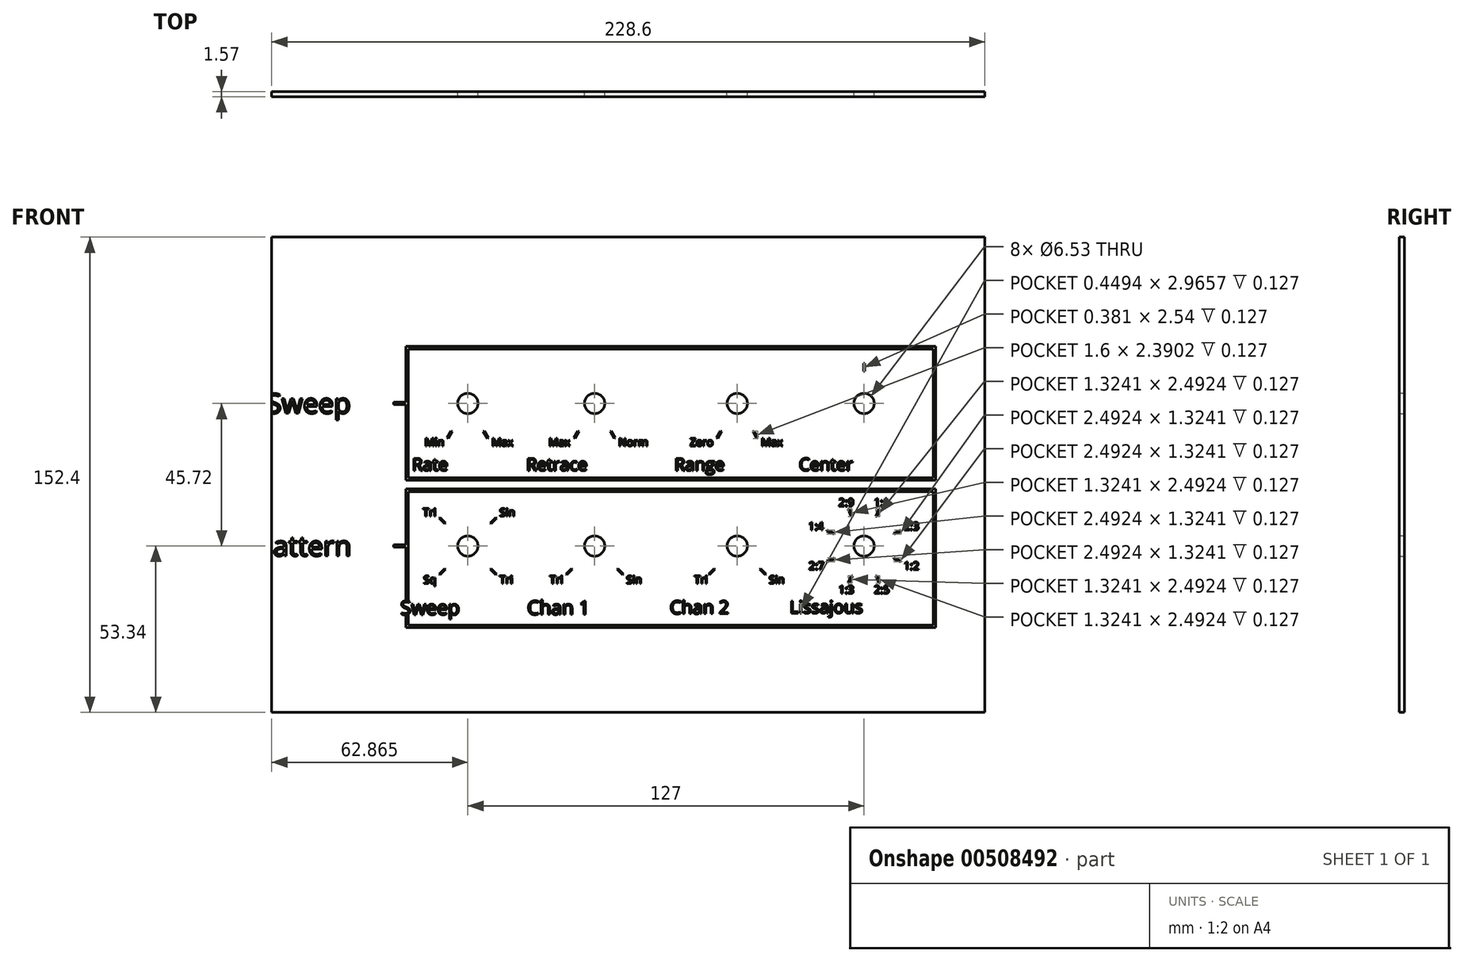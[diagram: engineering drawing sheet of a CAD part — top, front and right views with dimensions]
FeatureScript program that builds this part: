
annotation { "Feature Type Name" : "Feature", "Feature Type Description" : "" }
export const myFeature = defineFeature(function(context is Context, id is Id, definition is map)
    precondition{}
    {
        {
            var Q0;
            Q0=qCreatedBy(makeId("Front.planeOp"),FACE);
            var sketch = newSketch(context, id + "F0", { "sketchPlane" : qUnion([Q0])});
            skLineSegment(sketch, "E0.bottom", {"start": v(114.3, -76.2) * mm, "end": v(-114.3, -76.2) * mm});
            skLineSegment(sketch, "E0.top", {"start": v(114.3, 76.2) * mm, "end": v(-114.3, 76.2) * mm});
            skLineSegment(sketch, "E0.left", {"start": v(114.3, -76.2) * mm, "end": v(114.3, 76.2) * mm});
            skLineSegment(sketch, "E0.right", {"start": v(-114.3, -76.2) * mm, "end": v(-114.3, 76.2) * mm});
            skPoint(sketch, "E0.middle", {"position": v(0, 0) * mm});
            skSolve(sketch);
        }
        {
            var Q0;
            Q0 = qSketchRegion(id + "F0", true);
            extrude(context, id + "F1", {"entities" : qUnion([Q0]), "depth" : 1.57 * mm});
        }
        {
            var Q0;
            Q0=makeQuery(id+"F1.opExtrude","CAP_FACE",FACE,{"disambiguationData":[OSD([sQuery(id+"F0.wireOp",EDGE,"E0.bottom"),sQuery(id+"F0.wireOp",EDGE,"E0.top"),sQuery(id+"F0.wireOp",EDGE,"E0.left"),sQuery(id+"F0.wireOp",EDGE,"E0.right")])],"isStart":false});
            var sketch = newSketch(context, id + "F2", { "sketchPlane" : qUnion([Q0])});
            skLineSegment(sketch, "E1", {"start": v(0, 117.54) * mm, "end": v(0, -147.27) * mm, "construction": true});
            skPoint(sketch, "E1.startSnap0", {"position": v(0, 76.2) * mm});
            skLineSegment(sketch, "E2", {"start": v(-154.79, 0) * mm, "end": v(171.18, 0) * mm, "construction": true});
            skPoint(sketch, "E2.endSnap0", {"position": v(114.3, 0) * mm});
            skLineSegment(sketch, "E3", {"start": v(-51.44, 120.6) * mm, "end": v(-51.43, -147.27) * mm, "construction": true});
            skLineSegment(sketch, "E4", {"start": v(-10.8, 117.54) * mm, "end": v(-10.8, -147.27) * mm, "construction": true});
            skLineSegment(sketch, "E5", {"start": v(34.93, 117.54) * mm, "end": v(34.93, -147.27) * mm, "construction": true});
            skLineSegment(sketch, "E6", {"start": v(75.57, 117.54) * mm, "end": v(75.57, -147.27) * mm, "construction": true});
            skLineSegment(sketch, "E7", {"start": v(-154.79, 22.86) * mm, "end": v(171.18, 22.86) * mm, "construction": true});
            skLineSegment(sketch, "E8", {"start": v(-154.79, -22.86) * mm, "end": v(171.18, -22.86) * mm, "construction": true});
            skPoint(sketch, "E9", {"position": v(-51.44, 22.86) * mm});
            skPoint(sketch, "E10", {"position": v(-10.8, 22.86) * mm});
            skPoint(sketch, "E11", {"position": v(34.93, 22.86) * mm});
            skPoint(sketch, "E12", {"position": v(75.57, 22.86) * mm});
            skPoint(sketch, "E13", {"position": v(75.57, -22.86) * mm});
            skPoint(sketch, "E14", {"position": v(34.93, -22.86) * mm});
            skPoint(sketch, "E15", {"position": v(-10.8, -22.86) * mm});
            skPoint(sketch, "E16", {"position": v(-51.43, -22.86) * mm});
            skSolve(sketch);
        }
        {
            var Q0;
            Q0=sQuery(id+"F2.wireOp",VERTEX,"E9");
            var Q1;
            Q1=sQuery(id+"F2.wireOp",VERTEX,"E10");
            var Q2;
            Q2=sQuery(id+"F2.wireOp",VERTEX,"E11");
            var Q3;
            Q3=sQuery(id+"F2.wireOp",VERTEX,"E12");
            var Q4;
            Q4=sQuery(id+"F2.wireOp",VERTEX,"E13");
            var Q5;
            Q5=sQuery(id+"F2.wireOp",VERTEX,"E14");
            var Q6;
            Q6=sQuery(id+"F2.wireOp",VERTEX,"E15");
            var Q7;
            Q7=sQuery(id+"F2.wireOp",VERTEX,"E16");
            var Q8;
            Q8=makeQuery(id+"F1.opExtrude","SWEPT_BODY",BODY,{"disambiguationData":[OSD([sQuery(id+"F0.wireOp",EDGE,"E0.bottom"),sQuery(id+"F0.wireOp",EDGE,"E0.top"),sQuery(id+"F0.wireOp",EDGE,"E0.left"),sQuery(id+"F0.wireOp",EDGE,"E0.right")])]});
            hole(context, id + "F3", {"style" : HoleStyle.SIMPLE, "endStyle" : HoleEndStyle.THROUGH, "holeDiameter" : 6.53 * mm, "tappedDepth" : 19.05 * mm, "tapClearance" : 3, "locations" : qUnion([Q0, Q1, Q2, Q3, Q4, Q5, Q6, Q7]), "scope" : qUnion([Q8]), "startStyle" : HoleStartStyle.PART});
        }
        {
            var Q0;
            Q0=makeQuery(id+"F1.opExtrude","CAP_FACE",FACE,{"disambiguationData":[OSD([sQuery(id+"F0.wireOp",EDGE,"E0.bottom"),sQuery(id+"F0.wireOp",EDGE,"E0.top"),sQuery(id+"F0.wireOp",EDGE,"E0.left"),sQuery(id+"F0.wireOp",EDGE,"E0.right")])],"isStart":false});
            var sketch = newSketch(context, id + "F4", { "sketchPlane" : qUnion([Q0])});
            skText(sketch, "E17", { "text": "Sweep", "fontName": "OpenSans-Regular.ttf"});
            skText(sketch, "E18", { "text": "Chan 1", "fontName": "OpenSans-Regular.ttf"});
            skLineSegment(sketch, "E19", {"start": v(-51.44, 22.86) * mm, "end": v(-51.43, -69.4) * mm, "construction": true});
            skLineSegment(sketch, "E20", {"start": v(-10.8, 22.86) * mm, "end": v(-10.8, -69.78) * mm, "construction": true});
            skLineSegment(sketch, "E21", {"start": v(34.93, 22.86) * mm, "end": v(34.93, -69.78) * mm, "construction": true});
            skLineSegment(sketch, "E22", {"start": v(75.57, 22.86) * mm, "end": v(75.57, -65.32) * mm, "construction": true});
            skText(sketch, "E23", { "text": "Chan 2", "fontName": "OpenSans-Regular.ttf"});
            skText(sketch, "E24", { "text": "Lissajous", "fontName": "OpenSans-Regular.ttf"});
            skText(sketch, "E25", { "text": "Retrace", "fontName": "OpenSans-Regular.ttf"});
            skText(sketch, "E26", { "text": "Range", "fontName": "OpenSans-Regular.ttf"});
            skText(sketch, "E27", { "text": "Center", "fontName": "OpenSans-Regular.ttf"});
            skText(sketch, "E28", { "text": "Rate", "fontName": "OpenSans-Regular.ttf"});
            skLineSegment(sketch, "E29", {"start": v(-51.43, -22.86) * mm, "end": v(-101.2, -22.86) * mm, "construction": true});
            skLineSegment(sketch, "E30", {"start": v(-51.44, 22.86) * mm, "end": v(-100.19, 22.86) * mm, "construction": true});
            skText(sketch, "E31", { "text": "Sweep", "fontName": "OpenSans-Regular.ttf"});
            skText(sketch, "E32", { "text": "Pattern", "fontName": "OpenSans-Regular.ttf"});
            const initialGuessF4  = {"E17": [-0.07303, -0.04488, 1, 0, 0.00447], "E18": [-0.03238, -0.04485, 1, 0, 0.00444], "E23": [0.01334, -0.04462, 1, 0, 0.00421], "E24": [0.05173, -0.0444, 1, 0, 0.00399], "E25": [-0.03268, 0.00132, 1, 0, 0.00399], "E26": [0.0148, 0.00132, 1, 0, 0.00399], "E27": [0.0547, 0.00132, 1, 0, 0.00399], "E28": [-0.06932, 0.00132, 1, 0, 0.00399], "E31": [-0.11598, 0.01968, 1, 0, 0.00635], "E32": [-0.11916, -0.02604, 1, 0, 0.00635]};
            skSetInitialGuess(sketch, initialGuessF4);
            skSolve(sketch);
        }
        {
            var Q0;
            Q0 = qSketchRegion(id + "F4", true);
            extrude(context, id + "F5", {"entities" : qUnion([Q0]), "operationType" : NewBodyOperationType.REMOVE, "oppositeDirection" : true, "depth" : 0.13 * mm, "offsetDistance" : 25.4 * mm});
        }
        {
            var Q0;
            {var subQ0=sQuery(id+"F0.wireOp",EDGE,"E0.left");var subQ1=sQuery(id+"F0.wireOp",EDGE,"E0.top");var subQ2=sQuery(id+"F0.wireOp",EDGE,"E0.bottom");var subQ3=sQuery(id+"F0.wireOp",EDGE,"E0.right");Q0=makeQuery(id+"F5.boolean.opBoolean","SPLIT",FACE,{"disambiguationData":[TD([makeQuery(id+"F1.opExtrude","SWEPT_FACE",FACE,{"disambiguationData":[OSD([subQ2])]})])],"derivedFrom":makeQuery(id+"F1.opExtrude","CAP_FACE",FACE,{"disambiguationData":[OSD([subQ2,subQ1,subQ0,subQ3])],"isStart":false})});}
            var sketch = newSketch(context, id + "F6", { "sketchPlane" : qUnion([Q0])});
            skCircle(sketch, "E33", {"center": v(-51.43, -22.86) * mm, "radius": 10.32 * mm, "construction": true});
            skCircle(sketch, "E34", {"center": v(-51.43, -22.86) * mm, "radius": 12.7 * mm, "construction": true});
            skLineSegment(sketch, "E35", {"start": v(-51.43, -22.86) * mm, "end": v(-41.93, -13.35) * mm, "construction": true});
            skLineSegment(sketch, "E36", {"start": v(-51.43, -22.86) * mm, "end": v(-41.87, -32.42) * mm, "construction": true});
            skLineSegment(sketch, "E37", {"start": v(-51.43, -22.86) * mm, "end": v(-51.43, -8.06) * mm, "construction": true});
            skText(sketch, "E38", { "text": "Tri", "fontName": "OpenSans-Regular.ttf"});
            skLineSegment(sketch, "E39.bottom", {"start": v(-44, -30.02) * mm, "end": v(-42.2, -31.82) * mm});
            skLineSegment(sketch, "E39.top", {"start": v(-44.27, -30.29) * mm, "end": v(-42.48, -32.09) * mm});
            skLineSegment(sketch, "E39.left", {"start": v(-44, -30.02) * mm, "end": v(-44.27, -30.29) * mm});
            skLineSegment(sketch, "E39.right", {"start": v(-42.2, -31.82) * mm, "end": v(-42.48, -32.09) * mm});
            skLineSegment(sketch, "E40.bottom", {"start": v(-42.48, -13.63) * mm, "end": v(-44.27, -15.43) * mm});
            skLineSegment(sketch, "E40.top", {"start": v(-42.2, -13.9) * mm, "end": v(-44, -15.7) * mm});
            skLineSegment(sketch, "E40.left", {"start": v(-42.48, -13.63) * mm, "end": v(-42.2, -13.9) * mm});
            skLineSegment(sketch, "E40.right", {"start": v(-44.27, -15.43) * mm, "end": v(-44, -15.7) * mm});
            skCircle(sketch, "E41", {"center": v(75.57, -22.86) * mm, "radius": 10.32 * mm, "construction": true});
            skCircle(sketch, "E42", {"center": v(75.57, -22.86) * mm, "radius": 12.7 * mm, "construction": true});
            skLineSegment(sketch, "E43", {"start": v(75.57, -22.86) * mm, "end": v(75.57, 0) * mm, "construction": true});
            skLineSegment(sketch, "E44", {"start": v(75.57, -22.86) * mm, "end": v(84.9, -0.34) * mm, "construction": true});
            skLineSegment(sketch, "E45.1.0", {"start": v(75.57, -22.86) * mm, "end": v(66.24, -0.34) * mm, "construction": true});
            skLineSegment(sketch, "E45.2.0", {"start": v(75.57, -22.86) * mm, "end": v(53.05, -13.53) * mm, "construction": true});
            skLineSegment(sketch, "E45.3.0", {"start": v(75.57, -22.86) * mm, "end": v(53.05, -32.19) * mm, "construction": true});
            skLineSegment(sketch, "E45.4.0", {"start": v(75.57, -22.86) * mm, "end": v(66.24, -45.38) * mm, "construction": true});
            skLineSegment(sketch, "E45.5.0", {"start": v(75.57, -22.86) * mm, "end": v(84.9, -45.38) * mm, "construction": true});
            skLineSegment(sketch, "E45.6.0", {"start": v(75.57, -22.86) * mm, "end": v(98.08, -32.19) * mm, "construction": true});
            skLineSegment(sketch, "E45.7.0", {"start": v(75.57, -22.86) * mm, "end": v(98.08, -13.53) * mm, "construction": true});
            skLineSegment(sketch, "E46.bottom", {"start": v(79.34, -13.26) * mm, "end": v(80.3, -10.9) * mm});
            skLineSegment(sketch, "E46.top", {"start": v(79.69, -13.4) * mm, "end": v(80.66, -11.05) * mm});
            skLineSegment(sketch, "E46.left", {"start": v(79.34, -13.26) * mm, "end": v(79.69, -13.4) * mm});
            skLineSegment(sketch, "E46.right", {"start": v(80.3, -10.9) * mm, "end": v(80.66, -11.05) * mm});
            skLineSegment(sketch, "E47.1.0", {"start": v(85.17, -19.09) * mm, "end": v(87.52, -18.12) * mm});
            skLineSegment(sketch, "E47.1.1", {"start": v(85.02, -18.74) * mm, "end": v(87.37, -17.76) * mm});
            skLineSegment(sketch, "E47.1.2", {"start": v(87.37, -17.76) * mm, "end": v(87.52, -18.12) * mm});
            skLineSegment(sketch, "E47.1.3", {"start": v(85.02, -18.74) * mm, "end": v(85.17, -19.09) * mm});
            skLineSegment(sketch, "E47.2.0", {"start": v(85.02, -26.98) * mm, "end": v(87.37, -27.96) * mm});
            skLineSegment(sketch, "E47.2.1", {"start": v(85.17, -26.63) * mm, "end": v(87.52, -27.6) * mm});
            skLineSegment(sketch, "E47.2.2", {"start": v(87.52, -27.6) * mm, "end": v(87.37, -27.96) * mm});
            skLineSegment(sketch, "E47.2.3", {"start": v(85.17, -26.63) * mm, "end": v(85.02, -26.98) * mm});
            skLineSegment(sketch, "E47.3.0", {"start": v(79.34, -32.46) * mm, "end": v(80.3, -34.81) * mm});
            skLineSegment(sketch, "E47.3.1", {"start": v(79.69, -32.32) * mm, "end": v(80.66, -34.67) * mm});
            skLineSegment(sketch, "E47.3.2", {"start": v(80.66, -34.67) * mm, "end": v(80.3, -34.81) * mm});
            skLineSegment(sketch, "E47.3.3", {"start": v(79.69, -32.32) * mm, "end": v(79.34, -32.46) * mm});
            skLineSegment(sketch, "E47.4.0", {"start": v(71.44, -32.32) * mm, "end": v(70.47, -34.67) * mm});
            skLineSegment(sketch, "E47.4.1", {"start": v(71.8, -32.46) * mm, "end": v(70.82, -34.81) * mm});
            skLineSegment(sketch, "E47.4.2", {"start": v(70.82, -34.81) * mm, "end": v(70.47, -34.67) * mm});
            skLineSegment(sketch, "E47.4.3", {"start": v(71.8, -32.46) * mm, "end": v(71.44, -32.32) * mm});
            skLineSegment(sketch, "E47.5.0", {"start": v(65.96, -26.63) * mm, "end": v(63.61, -27.6) * mm});
            skLineSegment(sketch, "E47.5.1", {"start": v(66.1, -26.98) * mm, "end": v(63.76, -27.96) * mm});
            skLineSegment(sketch, "E47.5.2", {"start": v(63.76, -27.96) * mm, "end": v(63.61, -27.6) * mm});
            skLineSegment(sketch, "E47.5.3", {"start": v(66.1, -26.98) * mm, "end": v(65.96, -26.63) * mm});
            skLineSegment(sketch, "E47.6.0", {"start": v(66.1, -18.74) * mm, "end": v(63.76, -17.76) * mm});
            skLineSegment(sketch, "E47.6.1", {"start": v(65.96, -19.09) * mm, "end": v(63.61, -18.12) * mm});
            skLineSegment(sketch, "E47.6.2", {"start": v(63.61, -18.12) * mm, "end": v(63.76, -17.76) * mm});
            skLineSegment(sketch, "E47.6.3", {"start": v(65.96, -19.09) * mm, "end": v(66.1, -18.74) * mm});
            skLineSegment(sketch, "E47.7.0", {"start": v(71.8, -13.26) * mm, "end": v(70.82, -10.9) * mm});
            skLineSegment(sketch, "E47.7.1", {"start": v(71.44, -13.4) * mm, "end": v(70.47, -11.05) * mm});
            skLineSegment(sketch, "E47.7.2", {"start": v(70.47, -11.05) * mm, "end": v(70.82, -10.9) * mm});
            skLineSegment(sketch, "E47.7.3", {"start": v(71.44, -13.4) * mm, "end": v(71.8, -13.26) * mm});
            skLineSegment(sketch, "E47.anchor1", {"start": v(75.57, -22.86) * mm, "end": v(79.69, -13.4) * mm, "construction": true});
            skLineSegment(sketch, "E47.anchor2", {"start": v(75.57, -22.86) * mm, "end": v(71.8, -13.26) * mm, "construction": true});
            skText(sketch, "E48", { "text": "2:5", "fontName": "OpenSans-Regular.ttf"});
            skText(sketch, "E49", { "text": "1:3", "fontName": "OpenSans-Regular.ttf"});
            skText(sketch, "E50", { "text": "2:7", "fontName": "OpenSans-Regular.ttf"});
            skText(sketch, "E51", { "text": "1:4", "fontName": "OpenSans-Regular.ttf"});
            skText(sketch, "E52", { "text": "2:9", "fontName": "OpenSans-Regular.ttf"});
            skText(sketch, "E53", { "text": "1:1", "fontName": "OpenSans-Regular.ttf"});
            skText(sketch, "E54", { "text": "2:3", "fontName": "OpenSans-Regular.ttf"});
            skText(sketch, "E55", { "text": "1:2", "fontName": "OpenSans-Regular.ttf"});
            skLineSegment(sketch, "E56", {"start": v(-10.8, -22.86) * mm, "end": v(-10.8, -39.67) * mm, "construction": true});
            skLineSegment(sketch, "E57", {"start": v(34.93, -22.86) * mm, "end": v(34.93, -39.28) * mm, "construction": true});
            skCircle(sketch, "E58", {"center": v(-10.8, -22.86) * mm, "radius": 10.32 * mm, "construction": true});
            skCircle(sketch, "E59", {"center": v(-10.8, -22.86) * mm, "radius": 12.7 * mm, "construction": true});
            skCircle(sketch, "E60", {"center": v(34.93, -22.86) * mm, "radius": 10.32 * mm, "construction": true});
            skCircle(sketch, "E61", {"center": v(34.93, -22.86) * mm, "radius": 12.7 * mm, "construction": true});
            skLineSegment(sketch, "E62", {"start": v(-51.43, -22.86) * mm, "end": v(-65.5, -36.92) * mm, "construction": true});
            skLineSegment(sketch, "E63", {"start": v(-10.8, -22.86) * mm, "end": v(-24.75, -36.82) * mm, "construction": true});
            skLineSegment(sketch, "E64", {"start": v(-10.8, -22.86) * mm, "end": v(3.44, -37.1) * mm, "construction": true});
            skLineSegment(sketch, "E65", {"start": v(34.93, -22.86) * mm, "end": v(21.23, -36.55) * mm, "construction": true});
            skLineSegment(sketch, "E66", {"start": v(34.93, -22.86) * mm, "end": v(49.67, -37.6) * mm, "construction": true});
            skLineSegment(sketch, "E67.bottom", {"start": v(25.7, -31.82) * mm, "end": v(27.5, -30.02) * mm});
            skLineSegment(sketch, "E67.top", {"start": v(25.97, -32.09) * mm, "end": v(27.76, -30.29) * mm});
            skLineSegment(sketch, "E67.left", {"start": v(25.7, -31.82) * mm, "end": v(25.97, -32.09) * mm});
            skLineSegment(sketch, "E67.right", {"start": v(27.5, -30.02) * mm, "end": v(27.76, -30.29) * mm});
            skLineSegment(sketch, "E68.bottom", {"start": v(42.35, -30.02) * mm, "end": v(44.15, -31.82) * mm});
            skLineSegment(sketch, "E68.top", {"start": v(42.09, -30.29) * mm, "end": v(43.88, -32.09) * mm});
            skLineSegment(sketch, "E68.left", {"start": v(42.35, -30.02) * mm, "end": v(42.09, -30.29) * mm});
            skLineSegment(sketch, "E68.right", {"start": v(44.15, -31.82) * mm, "end": v(43.88, -32.09) * mm});
            skLineSegment(sketch, "E69.bottom", {"start": v(-20.02, -31.82) * mm, "end": v(-18.22, -30.02) * mm});
            skLineSegment(sketch, "E69.top", {"start": v(-19.75, -32.09) * mm, "end": v(-17.96, -30.29) * mm});
            skLineSegment(sketch, "E69.left", {"start": v(-20.02, -31.82) * mm, "end": v(-19.75, -32.09) * mm});
            skLineSegment(sketch, "E69.right", {"start": v(-18.22, -30.02) * mm, "end": v(-17.96, -30.29) * mm});
            skLineSegment(sketch, "E70.bottom", {"start": v(-3.37, -30.02) * mm, "end": v(-1.57, -31.82) * mm});
            skLineSegment(sketch, "E70.top", {"start": v(-3.63, -30.29) * mm, "end": v(-1.84, -32.09) * mm});
            skLineSegment(sketch, "E70.left", {"start": v(-3.37, -30.02) * mm, "end": v(-3.63, -30.29) * mm});
            skLineSegment(sketch, "E70.right", {"start": v(-1.57, -31.82) * mm, "end": v(-1.84, -32.09) * mm});
            skLineSegment(sketch, "E71.bottom", {"start": v(-60.66, -31.82) * mm, "end": v(-58.86, -30.02) * mm});
            skLineSegment(sketch, "E71.top", {"start": v(-60.4, -32.09) * mm, "end": v(-58.6, -30.29) * mm});
            skLineSegment(sketch, "E71.left", {"start": v(-60.66, -31.82) * mm, "end": v(-60.4, -32.09) * mm});
            skLineSegment(sketch, "E71.right", {"start": v(-58.86, -30.02) * mm, "end": v(-58.6, -30.29) * mm});
            skText(sketch, "E72", { "text": "Sin", "fontName": "OpenSans-Regular.ttf"});
            skText(sketch, "E73", { "text": "Sq", "fontName": "OpenSans-Regular.ttf"});
            skText(sketch, "E74", { "text": "Tri", "fontName": "OpenSans-Regular.ttf"});
            skText(sketch, "E75", { "text": "Sin", "fontName": "OpenSans-Regular.ttf"});
            skText(sketch, "E76", { "text": "Sin", "fontName": "OpenSans-Regular.ttf"});
            skText(sketch, "E77", { "text": "Tri", "fontName": "OpenSans-Regular.ttf"});
            skCircle(sketch, "E78", {"center": v(-51.44, 22.86) * mm, "radius": 10.32 * mm, "construction": true});
            skCircle(sketch, "E79", {"center": v(-51.44, 22.86) * mm, "radius": 12.7 * mm, "construction": true});
            skCircle(sketch, "E80", {"center": v(-10.8, 22.86) * mm, "radius": 10.32 * mm, "construction": true});
            skCircle(sketch, "E81", {"center": v(34.93, 22.86) * mm, "radius": 10.32 * mm, "construction": true});
            skCircle(sketch, "E82", {"center": v(75.57, 22.86) * mm, "radius": 10.32 * mm, "construction": true});
            skCircle(sketch, "E83", {"center": v(-10.8, 22.86) * mm, "radius": 12.7 * mm, "construction": true});
            skCircle(sketch, "E84", {"center": v(34.93, 22.86) * mm, "radius": 12.7 * mm, "construction": true});
            skCircle(sketch, "E85", {"center": v(75.57, 22.86) * mm, "radius": 12.7 * mm, "construction": true});
            skLineSegment(sketch, "E86", {"start": v(-10.8, 22.86) * mm, "end": v(-10.8, 0) * mm, "construction": true});
            skLineSegment(sketch, "E87", {"start": v(-10.8, 22.86) * mm, "end": v(-23.44, 0.97) * mm, "construction": true});
            skLineSegment(sketch, "E88", {"start": v(-10.8, 22.86) * mm, "end": v(2.14, 0.45) * mm, "construction": true});
            skLineSegment(sketch, "E89.bottom", {"start": v(-17.39, 11.82) * mm, "end": v(-16.12, 14.02) * mm});
            skLineSegment(sketch, "E89.top", {"start": v(-17.06, 11.63) * mm, "end": v(-15.79, 13.83) * mm});
            skLineSegment(sketch, "E89.left", {"start": v(-17.39, 11.82) * mm, "end": v(-17.06, 11.63) * mm});
            skLineSegment(sketch, "E89.right", {"start": v(-16.12, 14.02) * mm, "end": v(-15.79, 13.83) * mm});
            skLineSegment(sketch, "E90.bottom", {"start": v(-5.47, 14.02) * mm, "end": v(-4.2, 11.82) * mm});
            skLineSegment(sketch, "E90.top", {"start": v(-5.8, 13.83) * mm, "end": v(-4.53, 11.63) * mm});
            skLineSegment(sketch, "E90.left", {"start": v(-5.47, 14.02) * mm, "end": v(-5.8, 13.83) * mm});
            skLineSegment(sketch, "E90.right", {"start": v(-4.2, 11.82) * mm, "end": v(-4.53, 11.63) * mm});
            skText(sketch, "E91", { "text": "Norm", "fontName": "OpenSans-Regular.ttf"});
            skText(sketch, "E92", { "text": "Max", "fontName": "OpenSans-Regular.ttf"});
            skLineSegment(sketch, "E93", {"start": v(-51.43, 22.86) * mm, "end": v(-51.43, 6.58) * mm, "construction": true});
            skLineSegment(sketch, "E94", {"start": v(-51.44, 22.86) * mm, "end": v(-60.83, 6.58) * mm, "construction": true});
            skLineSegment(sketch, "E95", {"start": v(-51.44, 22.86) * mm, "end": v(-42.04, 6.58) * mm, "construction": true});
            skLineSegment(sketch, "E96.bottom", {"start": v(-58.03, 11.82) * mm, "end": v(-56.76, 14.02) * mm});
            skLineSegment(sketch, "E96.top", {"start": v(-57.7, 11.63) * mm, "end": v(-56.43, 13.83) * mm});
            skLineSegment(sketch, "E96.left", {"start": v(-58.03, 11.82) * mm, "end": v(-57.7, 11.63) * mm});
            skLineSegment(sketch, "E96.right", {"start": v(-56.76, 14.02) * mm, "end": v(-56.43, 13.83) * mm});
            skLineSegment(sketch, "E97.bottom", {"start": v(-46.11, 14.02) * mm, "end": v(-44.84, 11.82) * mm});
            skLineSegment(sketch, "E97.top", {"start": v(-46.44, 13.83) * mm, "end": v(-45.17, 11.63) * mm});
            skLineSegment(sketch, "E97.left", {"start": v(-46.11, 14.02) * mm, "end": v(-46.44, 13.83) * mm});
            skLineSegment(sketch, "E97.right", {"start": v(-44.84, 11.82) * mm, "end": v(-45.17, 11.63) * mm});
            skText(sketch, "E98", { "text": "Min", "fontName": "OpenSans-Regular.ttf"});
            skText(sketch, "E99", { "text": "Max", "fontName": "OpenSans-Regular.ttf"});
            skLineSegment(sketch, "E100", {"start": v(75.57, 22.86) * mm, "end": v(75.57, 41.9) * mm, "construction": true});
            skLineSegment(sketch, "E101.bottom", {"start": v(75.37, 35.72) * mm, "end": v(75.76, 35.72) * mm});
            skLineSegment(sketch, "E101.top", {"start": v(75.37, 33.18) * mm, "end": v(75.76, 33.18) * mm});
            skLineSegment(sketch, "E101.left", {"start": v(75.37, 35.72) * mm, "end": v(75.37, 33.18) * mm});
            skLineSegment(sketch, "E101.right", {"start": v(75.76, 35.72) * mm, "end": v(75.76, 33.18) * mm});
            skLineSegment(sketch, "E102", {"start": v(34.93, 22.86) * mm, "end": v(34.93, 3.94) * mm, "construction": true});
            skLineSegment(sketch, "E103", {"start": v(34.92, 22.86) * mm, "end": v(24, 3.94) * mm, "construction": true});
            skLineSegment(sketch, "E104", {"start": v(34.93, 22.86) * mm, "end": v(45.85, 3.94) * mm});
            skLineSegment(sketch, "E105.bottom", {"start": v(28.33, 11.82) * mm, "end": v(29.6, 14.02) * mm});
            skLineSegment(sketch, "E105.top", {"start": v(28.66, 11.63) * mm, "end": v(29.93, 13.83) * mm});
            skLineSegment(sketch, "E105.left", {"start": v(28.33, 11.82) * mm, "end": v(28.66, 11.63) * mm});
            skLineSegment(sketch, "E105.right", {"start": v(29.6, 14.02) * mm, "end": v(29.93, 13.83) * mm});
            skLineSegment(sketch, "E106.bottom", {"start": v(40.25, 14.02) * mm, "end": v(41.52, 11.82) * mm});
            skLineSegment(sketch, "E106.top", {"start": v(39.92, 13.83) * mm, "end": v(41.19, 11.63) * mm});
            skLineSegment(sketch, "E106.left", {"start": v(40.25, 14.02) * mm, "end": v(39.92, 13.83) * mm});
            skLineSegment(sketch, "E106.right", {"start": v(41.52, 11.82) * mm, "end": v(41.19, 11.63) * mm});
            skText(sketch, "E107", { "text": "Max", "fontName": "OpenSans-Regular.ttf"});
            skText(sketch, "E108", { "text": "Zero", "fontName": "OpenSans-Regular.ttf"});
            skLineSegment(sketch, "E109", {"start": v(-51.43, -22.86) * mm, "end": v(-63.42, -10.87) * mm, "construction": true});
            skLineSegment(sketch, "E110.bottom", {"start": v(-60.4, -13.63) * mm, "end": v(-58.6, -15.43) * mm});
            skLineSegment(sketch, "E110.top", {"start": v(-60.66, -13.9) * mm, "end": v(-58.86, -15.7) * mm});
            skLineSegment(sketch, "E110.left", {"start": v(-60.4, -13.63) * mm, "end": v(-60.66, -13.9) * mm});
            skLineSegment(sketch, "E110.right", {"start": v(-58.6, -15.43) * mm, "end": v(-58.86, -15.7) * mm});
            skText(sketch, "E111", { "text": "Tri", "fontName": "OpenSans-Regular.ttf"});
            const initialGuessF6  = {"E38": [-0.04127, -0.03493, 1, 0, 0.00254], "E48": [0.07874, -0.0381, 1, 0, 0.00254], "E49": [0.0674, -0.0381, 1, 0, 0.00254], "E50": [0.05784, -0.03048, 1, 0, 0.00254], "E51": [0.05773, -0.01778, 1, 0, 0.00254], "E52": [0.06738, -0.01016, 1, 0, 0.00254], "E53": [0.07874, -0.01016, 1, 0, 0.00254], "E54": [0.08827, -0.01778, 1, 0, 0.00254], "E55": [0.08827, -0.03048, 1, 0, 0.00254], "E72": [-0.04127, -0.01334, 1, 0, 0.00254], "E73": [-0.06562, -0.03493, 1, 0, 0.00254], "E74": [-0.0252, -0.03493, 1, 0, 0.00254], "E75": [-0.00063, -0.03493, 1, 0, 0.00254], "E76": [0.04509, -0.03493, 1, 0, 0.00254], "E77": [0.02116, -0.03493, 1, 0, 0.00254], "E91": [-0.00317, 0.0092, 1, 0, 0.00254], "E92": [-0.02557, 0.0092, 1, 0, 0.00254], "E98": [-0.06524, 0.0092, 1, 0, 0.00254], "E99": [-0.04381, 0.0092, 1, 0, 0.00254], "E107": [0.04255, 0.0092, 1, 0, 0.00254], "E108": [0.01971, 0.0092, 1, 0, 0.00254], "E111": [-0.06583, -0.01334, 1, 0, 0.00254]};
            skSetInitialGuess(sketch, initialGuessF6);
            skSolve(sketch);
        }
        {
            var Q0;
            Q0 = qSketchRegion(id + "F6", true);
            extrude(context, id + "F7", {"entities" : qUnion([Q0]), "operationType" : NewBodyOperationType.REMOVE, "oppositeDirection" : true, "depth" : 0.13 * mm, "offsetDistance" : 25.4 * mm});
        }
        {
            var Q0;
            {var subQ0=sQuery(id+"F0.wireOp",EDGE,"E0.left");var subQ1=sQuery(id+"F0.wireOp",EDGE,"E0.bottom");var subQ2=sQuery(id+"F0.wireOp",EDGE,"E0.right");var subQ3=sQuery(id+"F0.wireOp",EDGE,"E0.top");Q0=makeQuery(id+"F5.boolean.opBoolean","SPLIT",FACE,{"disambiguationData":[TD([makeQuery(id+"F1.opExtrude","SWEPT_FACE",FACE,{"disambiguationData":[OSD([subQ1])]})])],"derivedFrom":makeQuery(id+"F1.opExtrude","CAP_FACE",FACE,{"disambiguationData":[OSD([subQ1,subQ3,subQ0,subQ2])],"isStart":false})});}
            var sketch = newSketch(context, id + "F8", { "sketchPlane" : qUnion([Q0])});
            skLineSegment(sketch, "E112.bottom", {"start": v(-70.48, 40.32) * mm, "end": v(97.8, 40.32) * mm});
            skLineSegment(sketch, "E112.top", {"start": v(-70.48, -0.95) * mm, "end": v(97.8, -0.95) * mm});
            skLineSegment(sketch, "E112.left", {"start": v(-70.48, 40.32) * mm, "end": v(-70.48, -0.95) * mm});
            skLineSegment(sketch, "E112.right", {"start": v(97.8, 40.32) * mm, "end": v(97.8, -0.95) * mm});
            skLineSegment(sketch, "E113.bottom", {"start": v(-70.48, -5.4) * mm, "end": v(97.8, -5.4) * mm});
            skLineSegment(sketch, "E113.top", {"start": v(-70.48, -48.26) * mm, "end": v(97.8, -48.26) * mm});
            skLineSegment(sketch, "E113.left", {"start": v(-70.48, -5.4) * mm, "end": v(-70.48, -48.26) * mm});
            skLineSegment(sketch, "E113.right", {"start": v(97.8, -5.4) * mm, "end": v(97.8, -48.26) * mm});
            skLineSegment(sketch, "E114", {"start": v(-51.44, 22.86) * mm, "end": v(-51.43, -22.86) * mm, "construction": true});
            skLineSegment(sketch, "E115", {"start": v(75.57, 22.86) * mm, "end": v(75.57, -22.86) * mm, "construction": true});
            skLineSegment(sketch, "E116", {"start": v(-51.43, -22.86) * mm, "end": v(-116, -22.86) * mm, "construction": true});
            skLineSegment(sketch, "E117.0", {"start": v(-71.28, 41.12) * mm, "end": v(98.58, 41.12) * mm});
            skLineSegment(sketch, "E117.1", {"start": v(-71.28, 41.12) * mm, "end": v(-71.28, -1.75) * mm});
            skLineSegment(sketch, "E117.2", {"start": v(-71.28, -1.75) * mm, "end": v(98.58, -1.75) * mm});
            skLineSegment(sketch, "E117.3", {"start": v(98.58, 41.12) * mm, "end": v(98.58, -1.75) * mm});
            skLineSegment(sketch, "E118.0", {"start": v(-71.28, -4.6) * mm, "end": v(98.58, -4.6) * mm});
            skLineSegment(sketch, "E118.1", {"start": v(-71.28, -4.6) * mm, "end": v(-71.28, -49.05) * mm});
            skLineSegment(sketch, "E118.2", {"start": v(-71.28, -49.05) * mm, "end": v(98.58, -49.05) * mm});
            skLineSegment(sketch, "E118.3", {"start": v(98.58, -4.6) * mm, "end": v(98.58, -49.05) * mm});
            skLineSegment(sketch, "E119.bottom", {"start": v(-75.25, 23.26) * mm, "end": v(-71.28, 23.26) * mm});
            skLineSegment(sketch, "E119.top", {"start": v(-75.25, 22.46) * mm, "end": v(-71.28, 22.46) * mm});
            skLineSegment(sketch, "E119.left", {"start": v(-75.25, 23.26) * mm, "end": v(-75.25, 22.46) * mm});
            skLineSegment(sketch, "E119.right", {"start": v(-71.28, 23.26) * mm, "end": v(-71.28, 22.46) * mm});
            skLineSegment(sketch, "E120.bottom", {"start": v(-75.25, -22.46) * mm, "end": v(-71.28, -22.46) * mm});
            skLineSegment(sketch, "E120.top", {"start": v(-75.25, -23.26) * mm, "end": v(-71.28, -23.26) * mm});
            skLineSegment(sketch, "E120.left", {"start": v(-75.25, -22.46) * mm, "end": v(-75.25, -23.26) * mm});
            skLineSegment(sketch, "E120.right", {"start": v(-71.28, -22.46) * mm, "end": v(-71.28, -23.26) * mm});
            skLineSegment(sketch, "E121", {"start": v(-51.44, 22.86) * mm, "end": v(-112.61, 22.86) * mm, "construction": true});
            skSolve(sketch);
        }
        {
            var Q0;
            Q0=makeQuery(id+"F8.imprint","IMPRINT",FACE,{"disambiguationData":[TD([[makeQuery(id+"F8.imprint","IMPRINT",EDGE,{"derivedFrom":sQuery(id+"F8.wireOp",EDGE,"E112.bottom")}),1.0]])]});
            var Q1;
            Q1=makeQuery(id+"F8.imprint","IMPRINT",FACE,{"disambiguationData":[TD([[makeQuery(id+"F8.imprint","IMPRINT",EDGE,{"derivedFrom":sQuery(id+"F8.wireOp",EDGE,"E119.bottom")}),-1.0]])]});
            var Q2;
            Q2=makeQuery(id+"F8.imprint","IMPRINT",FACE,{"disambiguationData":[TD([[makeQuery(id+"F8.imprint","IMPRINT",EDGE,{"derivedFrom":sQuery(id+"F8.wireOp",EDGE,"E113.bottom")}),1.0]])]});
            var Q3;
            Q3=makeQuery(id+"F8.imprint","IMPRINT",FACE,{"disambiguationData":[TD([[makeQuery(id+"F8.imprint","IMPRINT",EDGE,{"derivedFrom":sQuery(id+"F8.wireOp",EDGE,"E120.bottom")}),-1.0]])]});
            extrude(context, id + "F9", {"entities" : qUnion([Q0, Q1, Q2, Q3]), "operationType" : NewBodyOperationType.REMOVE, "oppositeDirection" : true, "depth" : 0.13 * mm, "offsetDistance" : 25.4 * mm});
        }
    });
